# Revit family: 0005310
name_source: partatom
category: Lighting Fixtures
revit_build: Autodesk Revit 2017 (Build: 20160225_1515(x64)
units: mm (PartAtom-declared; Revit-internal decimal feet)

## family parameters
Cut with Voids When Loaded = No
Host = Face
Light Source = No
OmniClass Number = 23.80.70.00
OmniClass Title = Lighting
Part Type = Normal
Room Calculation Point = No
Round Connector Dimension = Use Diameter
Shared = No

## types (6) — shared parameters
Apparent Load = 0 VA
Assembly Code = D5020200
AssetType = Fixed
CircularCutOutDia_SYL = 39 mm
ClassificationName = Uniclass2015
ClassificationValue = EF_70_80
Default Elevation = 1219 mm
DocumentationLiterature = http://www.sylvania-lighting.com
ElectricShockClassification = Class II
HoleDist_SYL = 220 mm
IfcExportAs = IfcLightFixtureType
IfcExportType = IfcLightFixtureType
ImpactProtectionIndex = IK03
IngressProtection = IP20
InputNominalFrequency = 50/60 HZ
InputVoltage = 220-240 V AC
Keynote = 16500
Lamp = LED
LampColourRenderingIndex = 90
LampMacAdamStep = 3
LampsType = LED
Manufacturer = Feilo Sylvania
ManufacturerName = Feilo Sylvania
Material = aluminium housing
Material_1_SYL = PC/ABS Plastic
Material_2_SYL = <By Category>
Material_3_SYL = <By Category>
Material_4_SYL = <By Category>
NominalDepth = 110 mm  [stored 0.360892 ft]
NominalLength = 110 mm  [stored 0.360892 ft]
PowerConsumption = 12 W
PowerFactor = 0.9
RadiusTrim_SYL = 3 mm  [stored 0.00984252 ft]
RecessDepth_SYL = 100 mm  [stored 0.328084 ft]
RecessLength_SYL = 90 mm  [stored 0.295276 ft]
RecessWidth_SYL = 90 mm  [stored 0.295276 ft]
TrimHeight_SYL = 3 mm  [stored 0.00984252 ft]
TrimLength_SYL = 110 mm  [stored 0.360892 ft]
TrimWidth_SYL = 110 mm  [stored 0.360892 ft]
Type Image = <None>
TypeLamp_SYL = Ludospot 50 Modules : 0005301 Ludospot 50 950lm 930 NB DIM
URL = http://www.sylvania-lighting.com
Voltage = 0 V
WallThickness_SYL = 2 mm  [stored 0.00656168 ft]
zero-valued in all types: Cost, NominalHeight

## per-type parameters (varying)
| type | LampColourTemperature | LampNominalLuminous | LuminousEfficacy | Model | ModelNumber | ModelReference | Name | TypeName |
| 0005310+0005306 Ludospot 50 Hous SQR RECT X1 CRDNC WHT + Ludospot 50 940lm 940 WB DIM | 4000 K | 940 lm | 78 lm/W | Ludospot 50 Hous SQR RECT X1 CRDNC WHT + Ludospot 50 940lm 940 WB DIM | 0005310+0005306 | Ludospot 50 Hous SQR RECT X1 CRDNC WHT + Ludospot 50 940lm 940 WB DIM | Ludospot 50 Hous SQR RECT X1 CRDNC WHT + Ludospot 50 940lm 940 WB DIM | Ludospot 50 Hous SQR RECT X1 CRDNC WHT + Ludospot 50 940lm 940 WB DIM |
| 0005310+0005305 Ludospot 50 Hous SQR RECT X1 CRDNC WHT + Ludospot 50 920lm 930 WB DIM | 3000 K | 920 lm | 77 lm/W | Ludospot 50 Hous SQR RECT X1 CRDNC WHT + Ludospot 50 920lm 930 WB DIM | 0005310+0005305 | Ludospot 50 Hous SQR RECT X1 CRDNC WHT + Ludospot 50 920lm 930 WB DIM | Ludospot 50 Hous SQR RECT X1 CRDNC WHT + Ludospot 50 920lm 930 WB DIM | Ludospot 50 Hous SQR RECT X1 CRDNC WHT + Ludospot 50 920lm 930 WB DIM |
| 0005310+0005304 Ludospot 50 Hous SQR RECT X1 CRDNC WHT + Ludospot 50 1000lm 940 MB DIM | 4000 K | 950 lm | 83 lm/W | Ludospot 50 Hous SQR RECT X1 CRDNC WHT + Ludospot 50 1000lm 940 MB DIM | 0005310+0005304 | Ludospot 50 Hous SQR RECT X1 CRDNC WHT + Ludospot 50 1000lm 940 MB DIM | Ludospot 50 Hous SQR RECT X1 CRDNC WHT + Ludospot 50 1000lm 940 MB DIM | Ludospot 50 Hous SQR RECT X1 CRDNC WHT + Ludospot 50 1000lm 940 MB DIM |
| 0005310+0005303 Ludospot 50 Hous SQR RECT X1 CRDNC WHT + Ludospot 50 950lm 930 MB DIM | 3000 K | 1000 lm | 80 lm/W | Ludospot 50 Hous SQR RECT X1 CRDNC WHT + Ludospot 50 950lm 930 MB DIM | 0005310+0005303 | Ludospot 50 Hous SQR RECT X1 CRDNC WHT + Ludospot 50 950lm 930 MB DIM | Ludospot 50 Hous SQR RECT X1 CRDNC WHT + Ludospot 50 950lm 930 MB DIM | Ludospot 50 Hous SQR RECT X1 CRDNC WHT + Ludospot 50 950lm 930 MB DIM |
| 0005310+0005302 Ludospot 50 Hous SQR RECT X1 CRDNC WHT + Ludospot 50 990lm 940 NB DIM | 4000 K | 990 lm | 83 lm/W | Ludospot 50 Hous SQR RECT X1 CRDNC WHT + Ludospot 50 990lm 940 NB DIM | 0005310+0005302 | Ludospot 50 Hous SQR RECT X1 CRDNC WHT + Ludospot 50 990lm 940 NB DIM | Ludospot 50 Hous SQR RECT X1 CRDNC WHT + Ludospot 50 990lm 940 NB DIM | Ludospot 50 Hous SQR RECT X1 CRDNC WHT + Ludospot 50 990lm 940 NB DIM |
| 0005310+0005301 Ludospot 50 Hous SQR RECT X1 CRDNC WHT + Ludospot 50 950lm 930 NB DIM | 3000 K | 950 lm | 80 lm/W | Ludospot 50 Hous SQR RECT X1 CRDNC WHT + Ludospot 50 950lm 930 NB DIM | 0005310+0005301 | Ludospot 50 Hous SQR RECT X1 CRDNC WHT + Ludospot 50 950lm 930 NB DIM | Ludospot 50 Hous SQR RECT X1 CRDNC WHT + Ludospot 50 950lm 930 NB DIM | Ludospot 50 Hous SQR RECT X1 CRDNC WHT + Ludospot 50 950lm 930 NB DIM |

note: [stored X ft] marks values corroborated as IEEE doubles in the binary element streams (Revit-internal decimal feet)

## geometry (parser evidence)
native form markers: Sweep x7
no freeform markers — native parametric forms only
